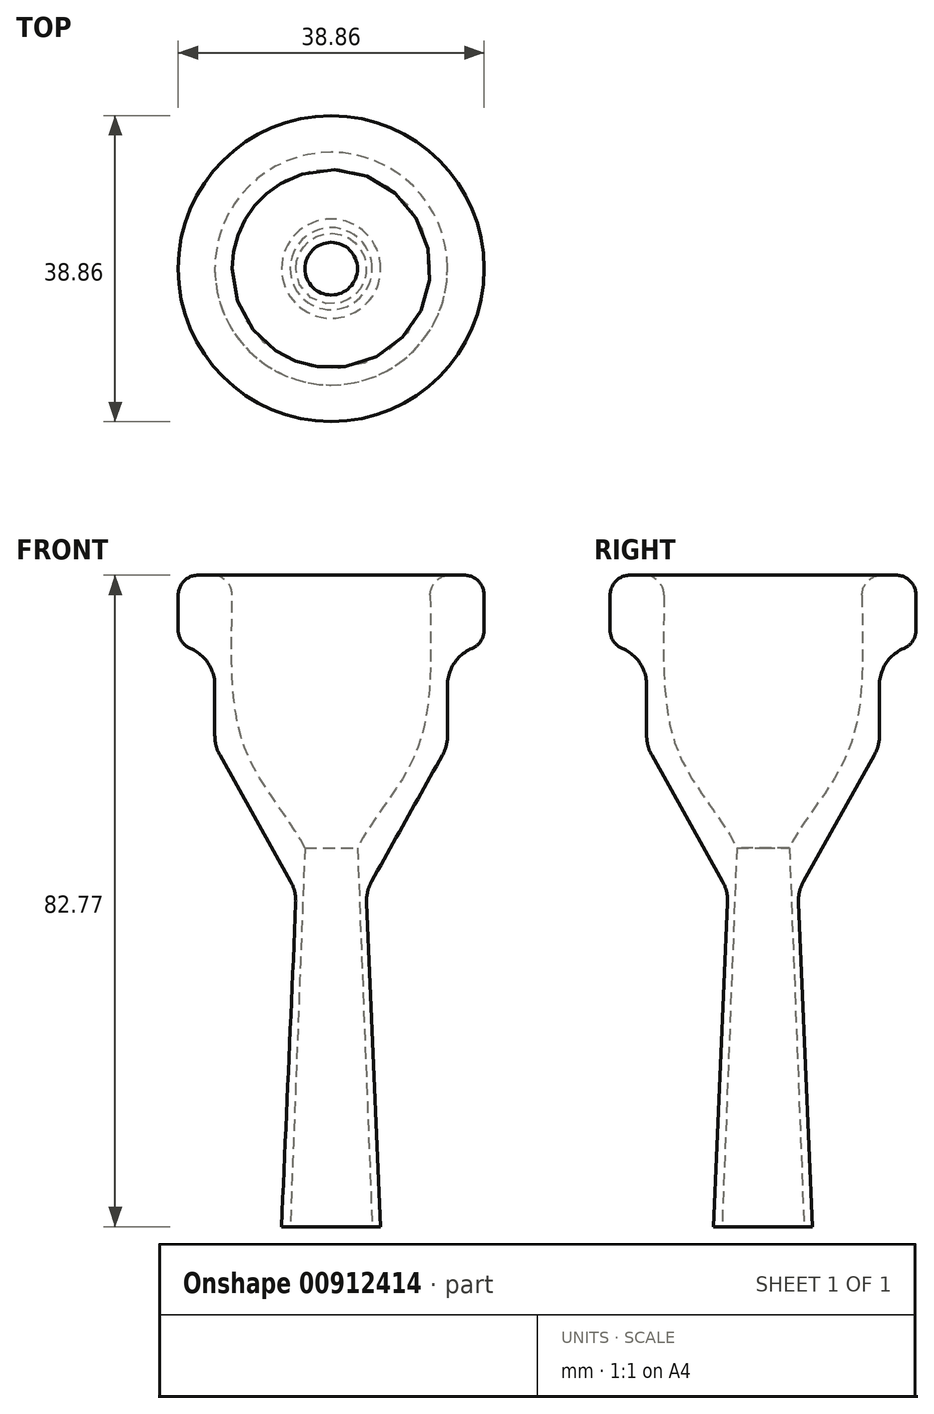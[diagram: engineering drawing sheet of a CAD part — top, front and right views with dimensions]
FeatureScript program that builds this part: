
annotation { "Feature Type Name" : "Feature", "Feature Type Description" : "" }
export const myFeature = defineFeature(function(context is Context, id is Id, definition is map)
    precondition{}
    {
        {
            var Q0;
            Q0=qCreatedBy(makeId("Right.planeOp"),FACE);
            var sketch = newSketch(context, id + "F0", { "sketchPlane" : qUnion([Q0])});
            skLineSegment(sketch, "E0", {"start": v(0, 0) * mm, "end": v(0, -48.12) * mm});
            skLineSegment(sketch, "E1", {"start": v(0, 0) * mm, "end": v(0, 34.65) * mm, "construction": true});
            skLineSegment(sketch, "E2.MirrorCS", {"start": v(-2.83, 0) * mm, "end": v(0, 0) * mm});
            skLineSegment(sketch, "E3", {"start": v(0, -48.12) * mm, "end": v(0, -42.34) * mm, "construction": true});
            skLineSegment(sketch, "E4", {"start": v(0, -42.34) * mm, "end": v(0, 0) * mm, "construction": true});
            skLineSegment(sketch, "E5", {"start": v(0, -48.12) * mm, "end": v(10.41, -48.12) * mm, "construction": true});
            skLineSegment(sketch, "E6.MirrorCS", {"start": v(0, -48.12) * mm, "end": v(-10.41, -48.12) * mm, "construction": true});
            skPoint(sketch, "E7.MirrorCS.start.orphan", {"position": v(0, 34.65) * mm});
            skLineSegment(sketch, "E8", {"start": v(4.43, -5.55) * mm, "end": v(6.3, -48.12) * mm});
            skLineSegment(sketch, "E9", {"start": v(5.2, -48.12) * mm, "end": v(6.3, -48.12) * mm});
            skPoint(sketch, "E10", {"position": v(3.34, 0) * mm});
            skLineSegment(sketch, "E11", {"start": v(0, 34.65) * mm, "end": v(12.57, 34.65) * mm, "construction": true});
            skFitSpline(sketch, "E12", {"points": [v(3.34, 0) * mm, v(11.05, 12.87) * mm, v(12.57, 34.65) * mm], "startDerivative": vector(12.86, 26.88) * mm, "endDerivative": vector(0.42, 41.85) * mm});
            skLineSegment(sketch, "E13", {"start": v(12.57, 34.65) * mm, "end": v(19.43, 34.65) * mm});
            skLineSegment(sketch, "E14", {"start": v(19.43, 34.65) * mm, "end": v(19.43, 25.14) * mm});
            skLineSegment(sketch, "E15", {"start": v(19.43, 25.14) * mm, "end": v(14.78, 25.14) * mm});
            skLineSegment(sketch, "E16", {"start": v(14.78, 25.14) * mm, "end": v(14.78, 12.94) * mm});
            skLineSegment(sketch, "E17", {"start": v(4.43, -5.55) * mm, "end": v(14.78, 12.94) * mm});
            skLineSegment(sketch, "E18", {"start": v(3.34, 0) * mm, "end": v(5.2, -48.12) * mm});
            skSolve(sketch);
        }
        {
            var Q0;
            Q0=makeQuery(id+"F0.imprint","IMPRINT",FACE,{"disambiguationData":[TD([[makeQuery(id+"F0.imprint","IMPRINT",EDGE,{"derivedFrom":sQuery(id+"F0.wireOp",EDGE,"E8")}),-1.0]])]});
            var Q1;
            Q1=sQuery(id+"F0.wireOp",EDGE,"E1");
            revolve(context, id + "F1", {"entities" : qUnion([Q0]), "axis" : qUnion([Q1]), "revolveType" : RevolveType.FULL});
        }
        {
            var Q0;
            Q0=makeQuery(id+"F1.opRevolve","SWEPT_EDGE",EDGE,{"disambiguationData":[OSD([sQuery(id+"F0.wireOp",EDGE,"E13"),sQuery(id+"F0.wireOp",EDGE,"E14")])]});
            var Q1;
            Q1=makeQuery(id+"F1.opRevolve","SWEPT_EDGE",EDGE,{"disambiguationData":[OSD([sQuery(id+"F0.wireOp",EDGE,"E12"),sQuery(id+"F0.wireOp",EDGE,"E13")])]});
            var Q2;
            Q2=makeQuery(id+"F1.opRevolve","SWEPT_EDGE",EDGE,{"disambiguationData":[OSD([sQuery(id+"F0.wireOp",EDGE,"E14"),sQuery(id+"F0.wireOp",EDGE,"E15")])]});
            fillet(context, id + "F2", {"entities" : qUnion([Q0, Q1, Q2]), "radius" : 2.54 * mm, "tangentPropagation" : true, "allowEdgeOverflow" : false});
        }
        {
            var Q0;
            Q0=makeQuery(id+"F1.opRevolve","SWEPT_EDGE",EDGE,{"disambiguationData":[OSD([sQuery(id+"F0.wireOp",EDGE,"E15"),sQuery(id+"F0.wireOp",EDGE,"E16")])]});
            var Q1;
            Q1=makeQuery(id+"F1.opRevolve","SWEPT_EDGE",EDGE,{"disambiguationData":[OSD([sQuery(id+"F0.wireOp",EDGE,"E16"),sQuery(id+"F0.wireOp",EDGE,"E17")])]});
            var Q2;
            Q2=makeQuery(id+"F1.opRevolve","SWEPT_FACE",FACE,{"disambiguationData":[OSD([sQuery(id+"F0.wireOp",EDGE,"E17")])]});
            fillet(context, id + "F3", {"entities" : qUnion([Q0, Q1, Q2]), "radius" : 5.08 * mm, "tangentPropagation" : true, "allowEdgeOverflow" : false});
        }
    });
